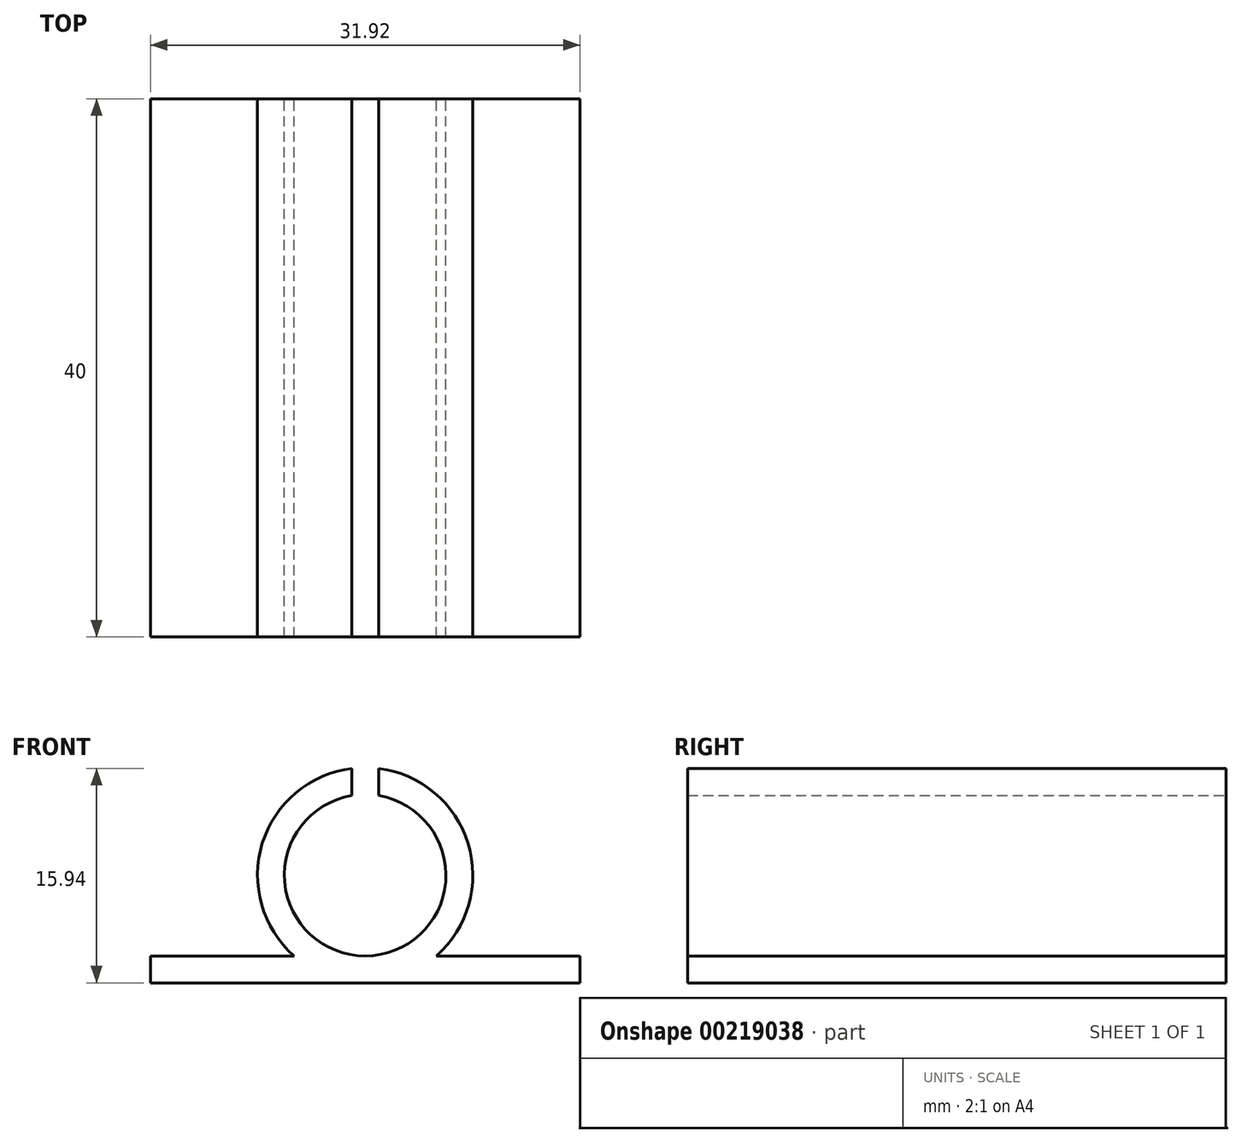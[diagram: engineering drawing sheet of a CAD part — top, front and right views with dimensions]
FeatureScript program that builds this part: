
annotation { "Feature Type Name" : "Feature", "Feature Type Description" : "" }
export const myFeature = defineFeature(function(context is Context, id is Id, definition is map)
    precondition{}
    {
        {
            var Q0;
            Q0=qCreatedBy(makeId("Front.planeOp"),FACE);
            var sketch = newSketch(context, id + "F0", { "sketchPlane" : qUnion([Q0])});
            skArc(sketch, "E0", {"start": v(-1, 5.92) * mm, "mid": v(0, -6) * mm, "end": v(1, 5.92) * mm});
            skArc(sketch, "E1.0", {"start": v(5.3, -6) * mm, "mid": v(7.65, 2.35) * mm, "end": v(1, 7.94) * mm});
            skLineSegment(sketch, "E2", {"start": v(5.3, -6) * mm, "end": v(15.96, -6) * mm});
            skLineSegment(sketch, "E3", {"start": v(15.96, -6) * mm, "end": v(15.96, -8) * mm});
            skLineSegment(sketch, "E4", {"start": v(15.96, -8) * mm, "end": v(0, -8) * mm});
            skLineSegment(sketch, "E5.MirrorCS", {"start": v(-5.3, -6) * mm, "end": v(-15.96, -6) * mm});
            skLineSegment(sketch, "E6.MirrorCS", {"start": v(-15.96, -8) * mm, "end": v(0, -8) * mm});
            skLineSegment(sketch, "E7.MirrorCS", {"start": v(-15.96, -6) * mm, "end": v(-15.96, -8) * mm});
            skPoint(sketch, "E8.orphan", {"position": v(0, -6) * mm});
            skLineSegment(sketch, "E9", {"start": v(0, 0) * mm, "end": v(0, 13.06) * mm, "construction": true});
            skPoint(sketch, "E9.endSnap0", {"position": v(0, 8) * mm});
            skLineSegment(sketch, "E10.0", {"start": v(1, 5.92) * mm, "end": v(1, 7.94) * mm});
            skLineSegment(sketch, "E11.0", {"start": v(-1, 5.92) * mm, "end": v(-1, 7.94) * mm});
            skArc(sketch, "E12.trimOffspring", {"start": v(-1, 7.94) * mm, "mid": v(-7.65, 2.35) * mm, "end": v(-5.3, -6) * mm});
            skSolve(sketch);
        }
        {
            var Q0;
            Q0=makeQuery(id+"F0.imprint","IMPRINT",FACE,{"disambiguationData":[TD([[makeQuery(id+"F0.imprint","IMPRINT",EDGE,{"derivedFrom":sQuery(id+"F0.wireOp",EDGE,"E0")}),-1.0]])]});
            extrude(context, id + "F1", {"entities" : qUnion([Q0]), "endBound" : BoundingType.SYMMETRIC, "depth" : 40 * mm});
        }
    });
